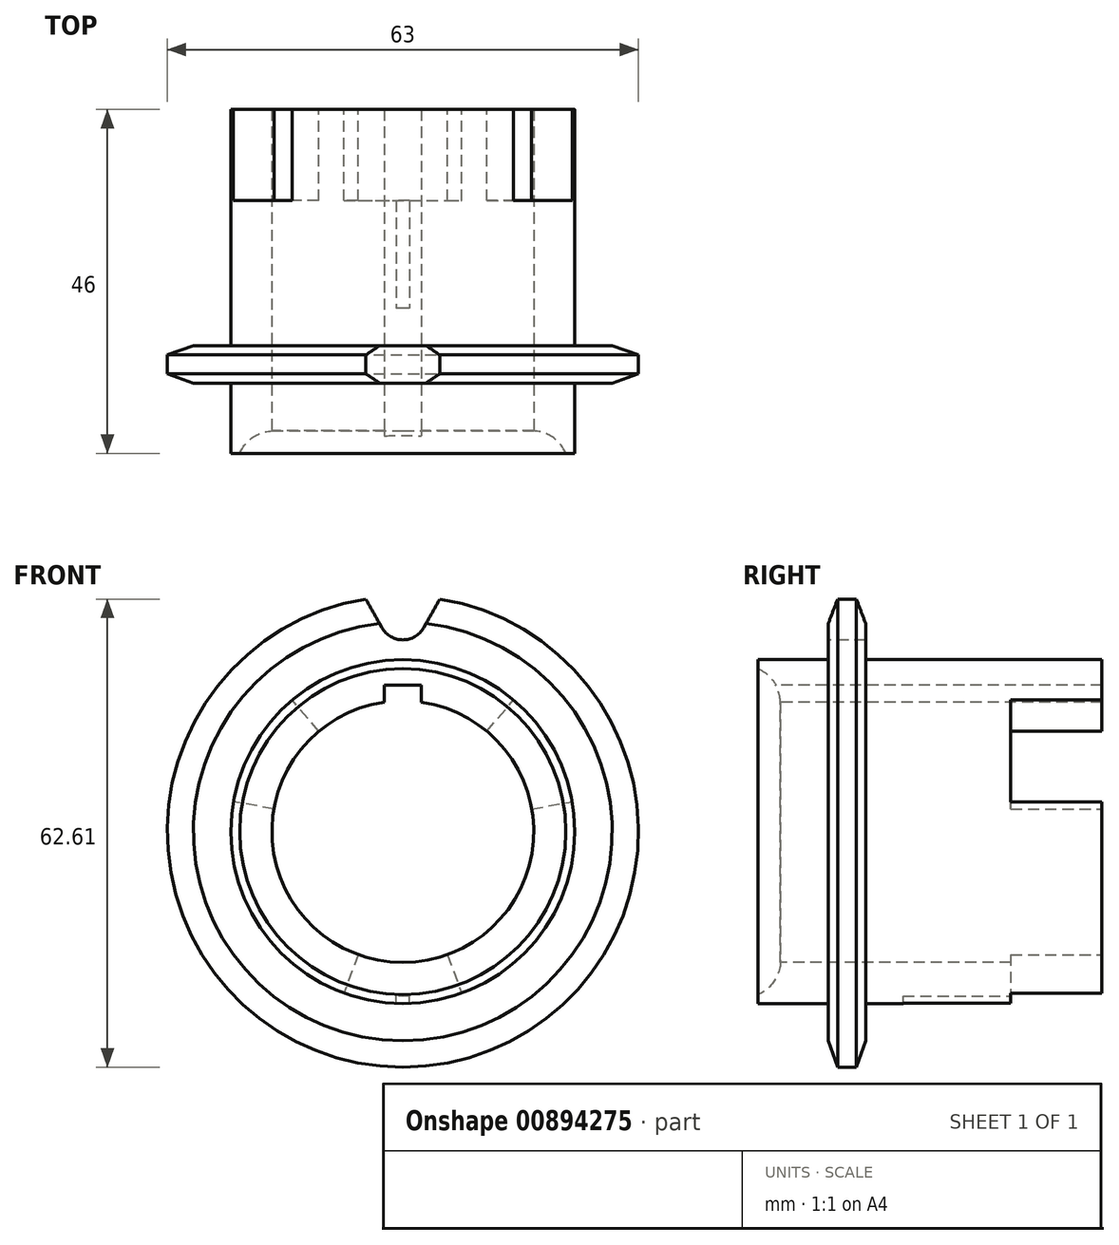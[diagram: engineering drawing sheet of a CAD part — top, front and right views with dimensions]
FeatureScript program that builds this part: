
annotation { "Feature Type Name" : "Feature", "Feature Type Description" : "" }
export const myFeature = defineFeature(function(context is Context, id is Id, definition is map)
    precondition{}
    {
        {
            var Q0;
            Q0=qCreatedBy(makeId("Right.planeOp"),FACE);
            var sketch = newSketch(context, id + "F0", { "sketchPlane" : qUnion([Q0])});
            skLineSegment(sketch, "E0", {"start": v(0, 0) * mm, "end": v(0, 17.5) * mm, "construction": true});
            skLineSegment(sketch, "E1", {"start": v(0, 17.5) * mm, "end": v(3, 17.5) * mm, "construction": true});
            skLineSegment(sketch, "E2", {"start": v(3, 17.5) * mm, "end": v(46, 17.5) * mm});
            skLineSegment(sketch, "E3", {"start": v(46, 17.5) * mm, "end": v(46, 23) * mm});
            skLineSegment(sketch, "E4", {"start": v(46, 23) * mm, "end": v(14.4, 23) * mm});
            skLineSegment(sketch, "E5", {"start": v(14.4, 23) * mm, "end": v(14.4, 28) * mm});
            skLineSegment(sketch, "E6", {"start": v(14.4, 28) * mm, "end": v(13.15, 31.5) * mm});
            skLineSegment(sketch, "E7", {"start": v(13.15, 31.5) * mm, "end": v(10.65, 31.5) * mm});
            skLineSegment(sketch, "E8", {"start": v(10.65, 31.5) * mm, "end": v(9.4, 28) * mm});
            skLineSegment(sketch, "E9", {"start": v(9.4, 28) * mm, "end": v(9.4, 23) * mm});
            skLineSegment(sketch, "E10", {"start": v(9.4, 23) * mm, "end": v(0, 23) * mm});
            skLineSegment(sketch, "E11", {"start": v(0, 23) * mm, "end": v(0, 21.8) * mm});
            skArc(sketch, "E12", {"start": v(3, 17.5) * mm, "mid": v(2.1, 20.07) * mm, "end": v(0, 21.8) * mm});
            skLineSegment(sketch, "E13", {"start": v(0, 0) * mm, "end": v(46, 0) * mm});
            skSolve(sketch);
        }
        {
            var Q0;
            Q0=makeQuery(id+"F0.imprint","IMPRINT",FACE,{"disambiguationData":[TD([[makeQuery(id+"F0.imprint","IMPRINT",EDGE,{"derivedFrom":sQuery(id+"F0.wireOp",EDGE,"E2")}),1.0]])]});
            var Q1;
            Q1=sQuery(id+"F0.wireOp",EDGE,"E13");
            revolve(context, id + "F1", {"surfaceOperationType" : NewSurfaceOperationType.NEW, "entities" : qUnion([Q0]), "axis" : qUnion([Q1]), "revolveType" : RevolveType.FULL});
        }
        {
            var Q0;
            Q0=qCreatedBy(makeId("Front.planeOp"),FACE);
            var sketch = newSketch(context, id + "F2", { "sketchPlane" : qUnion([Q0])});
            skLineSegment(sketch, "E14.bottom", {"start": v(-2.5, 14.6) * mm, "end": v(2.5, 14.6) * mm});
            skLineSegment(sketch, "E14.top", {"start": v(-2.5, 19.6) * mm, "end": v(2.5, 19.6) * mm});
            skLineSegment(sketch, "E14.left", {"start": v(-2.5, 14.6) * mm, "end": v(-2.5, 19.6) * mm});
            skLineSegment(sketch, "E14.right", {"start": v(2.5, 14.6) * mm, "end": v(2.5, 19.6) * mm});
            skLineSegment(sketch, "E15", {"start": v(0, 0) * mm, "end": v(0, 17.5) * mm, "construction": true});
            skLineSegment(sketch, "E16", {"start": v(0, 17.5) * mm, "end": v(0, 19.6) * mm, "construction": true});
            skSolve(sketch);
        }
        {
            var Q0;
            Q0=makeQuery(id+"F2.imprint","IMPRINT",FACE,{"disambiguationData":[TD([[makeQuery(id+"F2.imprint","IMPRINT",EDGE,{"derivedFrom":sQuery(id+"F2.wireOp",EDGE,"E14.bottom")}),1.0]])]});
            extrude(context, id + "F3", {"entities" : qUnion([Q0]), "operationType" : NewBodyOperationType.REMOVE, "endBound" : BoundingType.THROUGH_ALL, "oppositeDirection" : true, "depth" : 25 * mm, "offsetDistance" : 25 * mm});
        }
        {
            var Q0;
            Q0=makeQuery(id+"F1.opRevolve","SWEPT_FACE",FACE,{"disambiguationData":[OSD([sQuery(id+"F0.wireOp",EDGE,"E3")])]});
            var sketch = newSketch(context, id + "F4", { "sketchPlane" : qUnion([Q0])});
            skLineSegment(sketch, "E17", {"start": v(0, 0) * mm, "end": v(0, -23) * mm, "construction": true});
            skPoint(sketch, "E17.endSnap0", {"position": v(0, -17.5) * mm});
            skLineSegment(sketch, "E18", {"start": v(0, 0) * mm, "end": v(7.87, -21.61) * mm});
            skLineSegment(sketch, "E19", {"start": v(0, 0) * mm, "end": v(-7.87, -21.61) * mm});
            skArc(sketch, "E20", {"start": v(-7.87, -21.61) * mm, "mid": v(0, -23) * mm, "end": v(7.87, -21.61) * mm});
            skLineSegment(sketch, "E21.1.0", {"start": v(0, 0) * mm, "end": v(14.78, 17.62) * mm});
            skArc(sketch, "E21.1.1", {"start": v(22.65, 4) * mm, "mid": v(19.92, 11.5) * mm, "end": v(14.78, 17.62) * mm});
            skLineSegment(sketch, "E21.1.2", {"start": v(0, 0) * mm, "end": v(22.65, 4) * mm});
            skLineSegment(sketch, "E21.2.0", {"start": v(0, 0) * mm, "end": v(-22.65, 4) * mm});
            skArc(sketch, "E21.2.1", {"start": v(-14.78, 17.62) * mm, "mid": v(-19.92, 11.5) * mm, "end": v(-22.65, 4) * mm});
            skLineSegment(sketch, "E21.2.2", {"start": v(0, 0) * mm, "end": v(-14.78, 17.62) * mm});
            skSolve(sketch);
        }
        {
            var Q0;
            {var subQ0=sQuery(id+"F4.wireOp",EDGE,"E21.2.1");Q0=makeQuery(id+"F4.imprint","IMPRINT",FACE,{"disambiguationData":[TD([[makeQuery(id+"F4.imprint","IMPRINT",EDGE,{"derivedFrom":subQ0}),-1.0]])]});}
            var Q1;
            {var subQ0=sQuery(id+"F4.wireOp",EDGE,"E21.1.1");Q1=makeQuery(id+"F4.imprint","IMPRINT",FACE,{"disambiguationData":[TD([[makeQuery(id+"F4.imprint","IMPRINT",EDGE,{"derivedFrom":subQ0}),-1.0]])]});}
            var Q2;
            {var subQ0=sQuery(id+"F4.wireOp",EDGE,"E20");Q2=makeQuery(id+"F4.imprint","IMPRINT",FACE,{"disambiguationData":[TD([[makeQuery(id+"F4.imprint","IMPRINT",EDGE,{"derivedFrom":subQ0}),-1.0]])]});}
            extrude(context, id + "F5", {"entities" : qUnion([Q0, Q1, Q2]), "operationType" : NewBodyOperationType.REMOVE, "oppositeDirection" : true, "depth" : 12.2 * mm, "offsetDistance" : 25 * mm});
        }
        {
            var Q0;
            Q0=makeQuery(id+"F5.boolean.opBoolean","COPY",FACE,{"derivedFrom":makeQuery(id+"F5.opExtrude","CAP_FACE",FACE,{"disambiguationData":[OSD([sQuery(id+"F0.wireOp",EDGE,"E2"),sQuery(id+"F0.wireOp",EDGE,"E3"),sQuery(id+"F4.wireOp",EDGE,"E18"),sQuery(id+"F4.wireOp",EDGE,"E19"),sQuery(id+"F4.wireOp",EDGE,"E20")])],"isStart":false})});
            var sketch = newSketch(context, id + "F6", { "sketchPlane" : qUnion([Q0])});
            skLineSegment(sketch, "E22.bottom", {"start": v(-0.9, -23.8) * mm, "end": v(0.9, -23.8) * mm});
            skLineSegment(sketch, "E22.top", {"start": v(-0.9, -22) * mm, "end": v(0.9, -22) * mm});
            skLineSegment(sketch, "E22.left", {"start": v(-0.9, -23.8) * mm, "end": v(-0.9, -22) * mm});
            skLineSegment(sketch, "E22.right", {"start": v(0.9, -23.8) * mm, "end": v(0.9, -22) * mm});
            skLineSegment(sketch, "E23", {"start": v(0, 0) * mm, "end": v(0, -22) * mm, "construction": true});
            skSolve(sketch);
        }
        {
            var Q0;
            Q0 = qSketchRegion(id + "F6", true);
            extrude(context, id + "F7", {"entities" : qUnion([Q0]), "operationType" : NewBodyOperationType.REMOVE, "oppositeDirection" : true, "depth" : 14.4 * mm, "offsetDistance" : 25 * mm});
        }
        {
            var Q0;
            Q0=makeQuery(id+"F1.opRevolve","SWEPT_FACE",FACE,{"disambiguationData":[OSD([sQuery(id+"F0.wireOp",EDGE,"E9")])]});
            var sketch = newSketch(context, id + "F8", { "sketchPlane" : qUnion([Q0])});
            skLineSegment(sketch, "E24", {"start": v(4.95, 31.1) * mm, "end": v(2.79, 27.28) * mm});
            skLineSegment(sketch, "E25", {"start": v(-4.95, 31.1) * mm, "end": v(-2.79, 27.28) * mm});
            skArc(sketch, "E26", {"start": v(-2.79, 27.28) * mm, "mid": v(0, 25.65) * mm, "end": v(2.79, 27.28) * mm});
            skLineSegment(sketch, "E27", {"start": v(0, 28.85) * mm, "end": v(0, 0) * mm, "construction": true});
            skArc(sketch, "E28", {"start": v(4.95, 31.1) * mm, "mid": v(0, 31.5) * mm, "end": v(-4.95, 31.1) * mm});
            skSolve(sketch);
        }
        {
            var Q0;
            Q0 = qSketchRegion(id + "F8", true);
            extrude(context, id + "F9", {"entities" : qUnion([Q0]), "operationType" : NewBodyOperationType.REMOVE, "endBound" : BoundingType.THROUGH_ALL, "oppositeDirection" : true, "depth" : 25 * mm, "offsetDistance" : 25 * mm});
        }
    });
